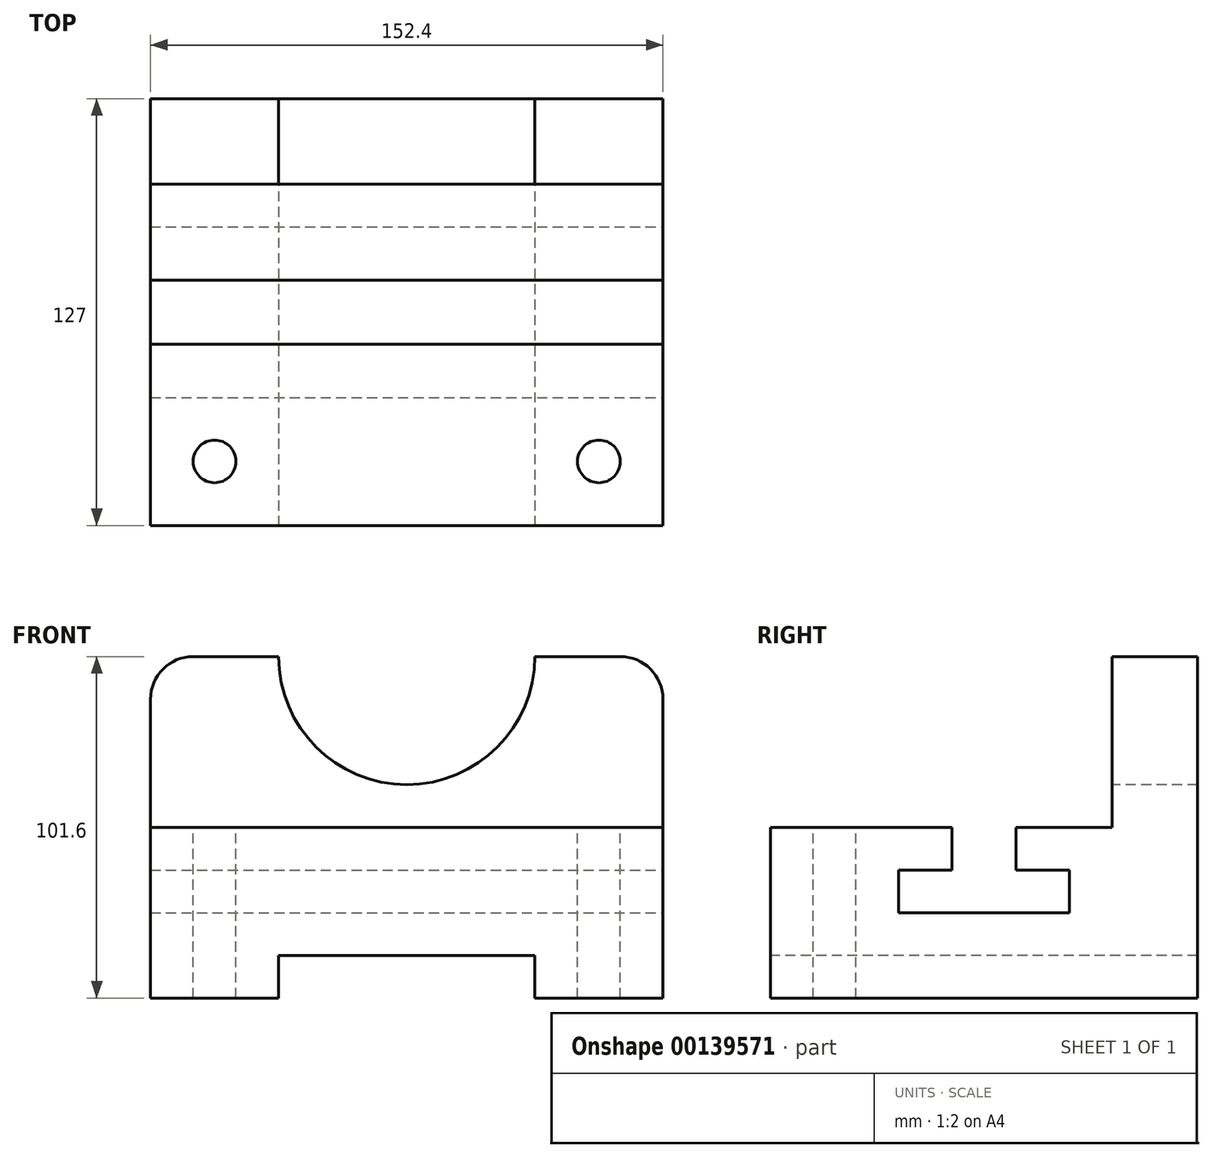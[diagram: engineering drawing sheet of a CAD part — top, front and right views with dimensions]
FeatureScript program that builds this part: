
annotation { "Feature Type Name" : "Feature", "Feature Type Description" : "" }
export const myFeature = defineFeature(function(context is Context, id is Id, definition is map)
    precondition{}
    {
        {
            var Q0;
            Q0=qCreatedBy(makeId("Front.planeOp"),FACE);
            var sketch = newSketch(context, id + "F0", { "sketchPlane" : qUnion([Q0])});
            skLineSegment(sketch, "E0.bottom", {"start": v(0, 101.6) * mm, "end": v(152.4, 101.6) * mm});
            skLineSegment(sketch, "E0.top", {"start": v(0, 0) * mm, "end": v(152.4, 0) * mm});
            skLineSegment(sketch, "E0.left", {"start": v(0, 101.6) * mm, "end": v(0, 0) * mm});
            skLineSegment(sketch, "E0.right", {"start": v(152.4, 101.6) * mm, "end": v(152.4, 0) * mm});
            skSolve(sketch);
        }
        {
            var Q0;
            Q0=makeQuery(id+"F0.imprint","IMPRINT",FACE,{"disambiguationData":[TD([[makeQuery(id+"F0.imprint","IMPRINT",EDGE,{"derivedFrom":sQuery(id+"F0.wireOp",EDGE,"E0.bottom")}),-1.0]])]});
            extrude(context, id + "F1", {"entities" : qUnion([Q0]), "depth" : 127 * mm});
        }
        {
            var Q0;
            Q0=makeQuery(id+"F1.opExtrude","CAP_FACE",FACE,{"disambiguationData":[OSD([sQuery(id+"F0.wireOp",EDGE,"E0.bottom"),sQuery(id+"F0.wireOp",EDGE,"E0.top"),sQuery(id+"F0.wireOp",EDGE,"E0.left"),sQuery(id+"F0.wireOp",EDGE,"E0.right")])],"isStart":false});
            var sketch = newSketch(context, id + "F2", { "sketchPlane" : qUnion([Q0])});
            skLineSegment(sketch, "E1.bottom", {"start": v(0, 101.6) * mm, "end": v(152.4, 101.6) * mm});
            skLineSegment(sketch, "E1.top", {"start": v(0, 50.8) * mm, "end": v(152.4, 50.8) * mm});
            skLineSegment(sketch, "E1.left", {"start": v(0, 101.6) * mm, "end": v(0, 50.8) * mm});
            skLineSegment(sketch, "E1.right", {"start": v(152.4, 101.6) * mm, "end": v(152.4, 50.8) * mm});
            skSolve(sketch);
        }
        {
            var Q0;
            Q0=makeQuery(id+"F2.imprint","IMPRINT",FACE,{"disambiguationData":[TD([[makeQuery(id+"F2.imprint","IMPRINT",EDGE,{"derivedFrom":sQuery(id+"F2.wireOp",EDGE,"E1.bottom")}),-1.0]])]});
            extrude(context, id + "F3", {"entities" : qUnion([Q0]), "operationType" : NewBodyOperationType.REMOVE, "oppositeDirection" : true, "depth" : 101.6 * mm});
        }
        {
            var Q0;
            Q0=makeQuery(id+"F3.boolean.opBoolean","COPY",FACE,{"derivedFrom":makeQuery(id+"F3.opExtrude","CAP_FACE",FACE,{"disambiguationData":[OSD([sQuery(id+"F2.wireOp",EDGE,"E1.bottom"),sQuery(id+"F2.wireOp",EDGE,"E1.top"),sQuery(id+"F2.wireOp",EDGE,"E1.left"),sQuery(id+"F2.wireOp",EDGE,"E1.right")])],"isStart":false})});
            var sketch = newSketch(context, id + "F4", { "sketchPlane" : qUnion([Q0])});
            skArc(sketch, "E2", {"start": v(38.1, 101.6) * mm, "mid": v(76.2, 63.5) * mm, "end": v(114.3, 101.6) * mm});
            skLineSegment(sketch, "E3", {"start": v(38.1, 101.6) * mm, "end": v(114.3, 101.6) * mm});
            skSolve(sketch);
        }
        {
            var Q0;
            Q0=makeQuery(id+"F4.imprint","IMPRINT",FACE,{"disambiguationData":[TD([[makeQuery(id+"F4.imprint","IMPRINT",EDGE,{"derivedFrom":sQuery(id+"F4.wireOp",EDGE,"E2")}),1.0]])]});
            extrude(context, id + "F5", {"entities" : qUnion([Q0]), "operationType" : NewBodyOperationType.REMOVE, "oppositeDirection" : true, "depth" : 25.4 * mm});
        }
        {
            var Q0;
            Q0=makeQuery(id+"F1.opExtrude","CAP_FACE",FACE,{"disambiguationData":[OSD([sQuery(id+"F0.wireOp",EDGE,"E0.bottom"),sQuery(id+"F0.wireOp",EDGE,"E0.top"),sQuery(id+"F0.wireOp",EDGE,"E0.left"),sQuery(id+"F0.wireOp",EDGE,"E0.right")])],"isStart":false});
            var sketch = newSketch(context, id + "F6", { "sketchPlane" : qUnion([Q0])});
            skLineSegment(sketch, "E4.bottom", {"start": v(38.1, 0) * mm, "end": v(114.3, 0) * mm});
            skLineSegment(sketch, "E4.top", {"start": v(38.1, 12.7) * mm, "end": v(114.3, 12.7) * mm});
            skLineSegment(sketch, "E4.left", {"start": v(38.1, 0) * mm, "end": v(38.1, 12.7) * mm});
            skLineSegment(sketch, "E4.right", {"start": v(114.3, 0) * mm, "end": v(114.3, 12.7) * mm});
            skSolve(sketch);
        }
        {
            var Q0;
            Q0=makeQuery(id+"F6.imprint","IMPRINT",FACE,{"disambiguationData":[TD([[makeQuery(id+"F6.imprint","IMPRINT",EDGE,{"derivedFrom":sQuery(id+"F6.wireOp",EDGE,"E4.bottom")}),1.0]])]});
            extrude(context, id + "F7", {"entities" : qUnion([Q0]), "operationType" : NewBodyOperationType.REMOVE, "endBound" : BoundingType.THROUGH_ALL, "oppositeDirection" : true, "depth" : 25.4 * mm});
        }
        {
            var Q0;
            Q0=makeQuery(id+"F1.opExtrude","SWEPT_FACE",FACE,{"disambiguationData":[OSD([sQuery(id+"F0.wireOp",EDGE,"E0.right")])]});
            var sketch = newSketch(context, id + "F8", { "sketchPlane" : qUnion([Q0])});
            skLineSegment(sketch, "E5", {"start": v(-73.03, 50.8) * mm, "end": v(-73.03, 38.1) * mm});
            skLineSegment(sketch, "E6", {"start": v(-73.03, 38.1) * mm, "end": v(-88.9, 38.1) * mm});
            skLineSegment(sketch, "E7", {"start": v(-88.9, 38.1) * mm, "end": v(-88.9, 25.4) * mm});
            skLineSegment(sketch, "E8", {"start": v(-88.9, 25.4) * mm, "end": v(-38.1, 25.4) * mm});
            skLineSegment(sketch, "E9", {"start": v(-38.1, 25.4) * mm, "end": v(-38.1, 38.1) * mm});
            skLineSegment(sketch, "E10", {"start": v(-38.1, 38.1) * mm, "end": v(-53.98, 38.1) * mm});
            skLineSegment(sketch, "E11", {"start": v(-53.98, 38.1) * mm, "end": v(-53.98, 50.8) * mm});
            skLineSegment(sketch, "E12", {"start": v(-53.98, 50.8) * mm, "end": v(-73.03, 50.8) * mm});
            skSolve(sketch);
        }
        {
            var Q0;
            Q0=makeQuery(id+"F8.imprint","IMPRINT",FACE,{"disambiguationData":[TD([[makeQuery(id+"F8.imprint","IMPRINT",EDGE,{"derivedFrom":sQuery(id+"F8.wireOp",EDGE,"E5")}),1.0]])]});
            extrude(context, id + "F9", {"entities" : qUnion([Q0]), "operationType" : NewBodyOperationType.REMOVE, "endBound" : BoundingType.THROUGH_ALL, "oppositeDirection" : true, "depth" : 25.4 * mm});
        }
        {
            var Q0;
            Q0=makeQuery(id+"F9.boolean.opBoolean","SPLIT",FACE,{"disambiguationData":[TD([makeQuery(id+"F9.opExtrude","SWEPT_FACE",FACE,{"disambiguationData":[OSD([sQuery(id+"F8.wireOp",EDGE,"E5")])]})])],"derivedFrom":makeQuery(id+"F3.boolean.opBoolean","COPY",FACE,{"derivedFrom":makeQuery(id+"F3.opExtrude","SWEPT_FACE",FACE,{"disambiguationData":[OSD([sQuery(id+"F2.wireOp",EDGE,"E1.top")])]})})});
            var sketch = newSketch(context, id + "F10", { "sketchPlane" : qUnion([Q0])});
            skLineSegment(sketch, "E13", {"start": v(76.2, -127) * mm, "end": v(76.2, -73.02) * mm, "construction": true});
            skCircle(sketch, "E14", {"center": v(19.05, -107.95) * mm, "radius": 6.35 * mm});
            skCircle(sketch, "E15.MirrorC", {"center": v(133.35, -107.95) * mm, "radius": 6.35 * mm});
            skSolve(sketch);
        }
        {
            var Q0;
            Q0 = qSketchRegion(id + "F10", true);
            extrude(context, id + "F11", {"entities" : qUnion([Q0]), "operationType" : NewBodyOperationType.REMOVE, "endBound" : BoundingType.THROUGH_ALL, "oppositeDirection" : true, "depth" : 25.4 * mm});
        }
        {
            var Q0;
            Q0=makeQuery(id+"F1.opExtrude","SWEPT_EDGE",EDGE,{"disambiguationData":[OSD([sQuery(id+"F0.wireOp",EDGE,"E0.bottom"),sQuery(id+"F0.wireOp",EDGE,"E0.right")])]});
            var Q1;
            Q1=makeQuery(id+"F1.opExtrude","SWEPT_EDGE",EDGE,{"disambiguationData":[OSD([sQuery(id+"F0.wireOp",EDGE,"E0.bottom"),sQuery(id+"F0.wireOp",EDGE,"E0.left")])]});
            fillet(context, id + "F12", {"entities" : qUnion([Q0, Q1]), "radius" : 12.7 * mm, "tangentPropagation" : true, "allowEdgeOverflow" : false});
        }
    });
